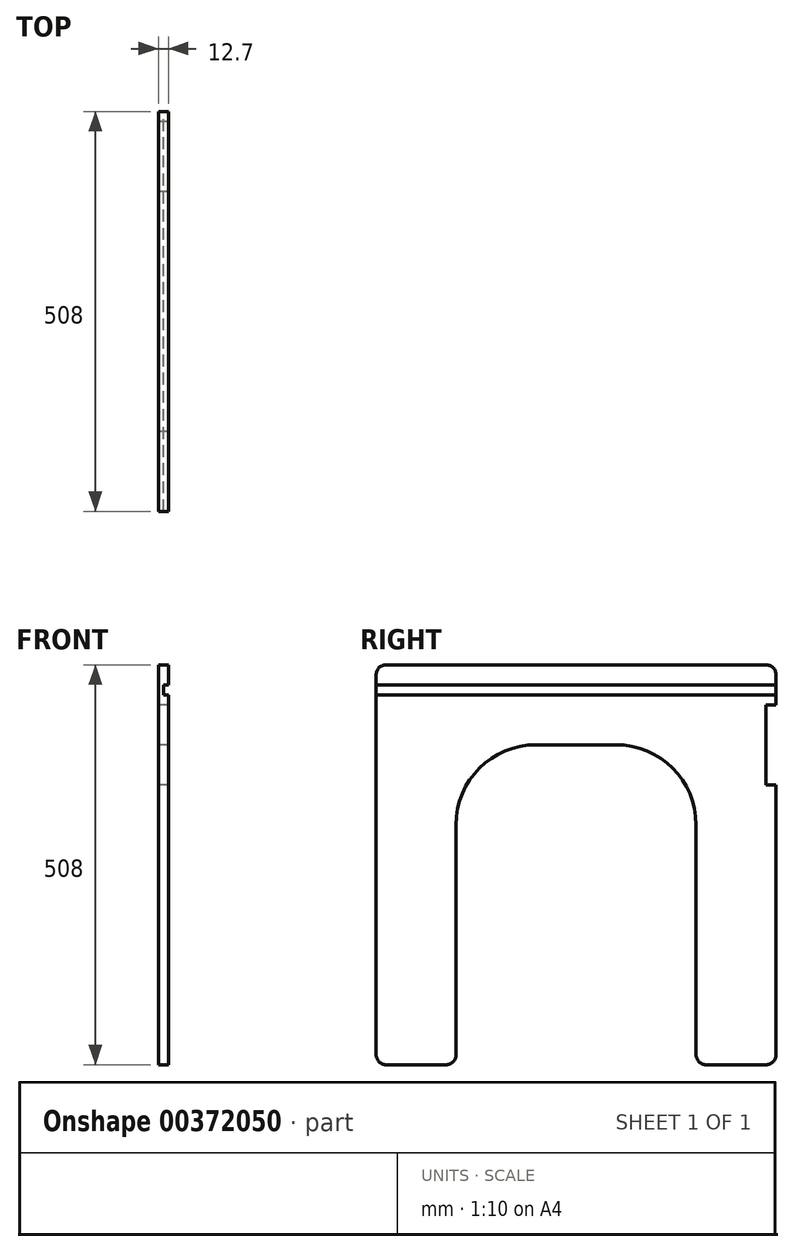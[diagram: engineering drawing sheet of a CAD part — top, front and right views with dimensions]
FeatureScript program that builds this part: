
annotation { "Feature Type Name" : "Feature", "Feature Type Description" : "" }
export const myFeature = defineFeature(function(context is Context, id is Id, definition is map)
    precondition{}
    {
        {
            var Q0;
            Q0=qCreatedBy(makeId("Right.planeOp"),FACE);
            var sketch = newSketch(context, id + "F0", { "sketchPlane" : qUnion([Q0])});
            skLineSegment(sketch, "E0.bottom", {"start": v(-88.9, 0) * mm, "end": v(-12.7, 0) * mm});
            skLineSegment(sketch, "E0.top", {"start": v(-88.9, 508) * mm, "end": v(393.7, 508) * mm});
            skLineSegment(sketch, "E0.left", {"start": v(-101.6, 12.7) * mm, "end": v(-101.6, 495.3) * mm});
            skLineSegment(sketch, "E0.right", {"start": v(406.4, 12.7) * mm, "end": v(406.4, 355.6) * mm});
            skLineSegment(sketch, "E1.top", {"start": v(203.2, 406.4) * mm, "end": v(101.6, 406.4) * mm});
            skLineSegment(sketch, "E1.left", {"start": v(304.8, 12.7) * mm, "end": v(304.8, 304.8) * mm});
            skLineSegment(sketch, "E1.right", {"start": v(0, 12.7) * mm, "end": v(0, 304.8) * mm});
            skPoint(sketch, "E2.visualSharp", {"position": v(0, 406.4) * mm});
            skArc(sketch, "E2.filletArc", {"start": v(101.6, 406.4) * mm, "mid": v(29.76, 376.64) * mm, "end": v(0, 304.8) * mm});
            skPoint(sketch, "E3.visualSharp", {"position": v(304.8, 406.4) * mm});
            skArc(sketch, "E3.filletArc", {"start": v(304.8, 304.8) * mm, "mid": v(275.04, 376.64) * mm, "end": v(203.2, 406.4) * mm});
            skPoint(sketch, "E4.visualSharp", {"position": v(-101.6, 0) * mm});
            skArc(sketch, "E4.filletArc", {"start": v(-101.6, 12.7) * mm, "mid": v(-97.88, 3.72) * mm, "end": v(-88.9, 0) * mm});
            skLineSegment(sketch, "E5.trimOffspring", {"start": v(317.5, 0) * mm, "end": v(393.7, 0) * mm});
            skPoint(sketch, "E6.visualSharp", {"position": v(0, 0) * mm});
            skArc(sketch, "E6.filletArc", {"start": v(-12.7, 0) * mm, "mid": v(-3.72, 3.72) * mm, "end": v(0, 12.7) * mm});
            skPoint(sketch, "E7.visualSharp", {"position": v(304.8, 0) * mm});
            skArc(sketch, "E7.filletArc", {"start": v(304.8, 12.7) * mm, "mid": v(308.52, 3.72) * mm, "end": v(317.5, 0) * mm});
            skPoint(sketch, "E8.visualSharp", {"position": v(406.4, 0) * mm});
            skArc(sketch, "E8.filletArc", {"start": v(393.7, 0) * mm, "mid": v(402.68, 3.72) * mm, "end": v(406.4, 12.7) * mm});
            skPoint(sketch, "E9.visualSharp", {"position": v(406.4, 508) * mm});
            skArc(sketch, "E9.filletArc", {"start": v(406.4, 495.3) * mm, "mid": v(402.68, 504.28) * mm, "end": v(393.7, 508) * mm});
            skPoint(sketch, "E10.visualSharp", {"position": v(-101.6, 508) * mm});
            skArc(sketch, "E10.filletArc", {"start": v(-88.9, 508) * mm, "mid": v(-97.88, 504.28) * mm, "end": v(-101.6, 495.3) * mm});
            skLineSegment(sketch, "E11.bottom", {"start": v(406.4, 457.2) * mm, "end": v(393.7, 457.2) * mm});
            skLineSegment(sketch, "E11.top", {"start": v(406.4, 355.6) * mm, "end": v(393.7, 355.6) * mm});
            skLineSegment(sketch, "E11.right", {"start": v(393.7, 457.2) * mm, "end": v(393.7, 355.6) * mm});
            skLineSegment(sketch, "E12.trimOffspring", {"start": v(406.4, 457.2) * mm, "end": v(406.4, 495.3) * mm});
            skSolve(sketch);
        }
        {
            var Q0;
            Q0=qSketchRegion(id+"F0",true);
            extrude(context, id + "F1", {"entities" : qUnion([Q0]), "depth" : 12.7 * mm});
        }
        {
            var Q0;
            Q0=makeQuery(id+"F1.opExtrude","CAP_FACE",FACE,{"disambiguationData":[OSD([sQuery(id+"F0.wireOp",EDGE,"E0.bottom"),sQuery(id+"F0.wireOp",EDGE,"E0.top"),sQuery(id+"F0.wireOp",EDGE,"E0.left"),sQuery(id+"F0.wireOp",EDGE,"E0.right"),sQuery(id+"F0.wireOp",EDGE,"E1.top"),sQuery(id+"F0.wireOp",EDGE,"E1.left"),sQuery(id+"F0.wireOp",EDGE,"E1.right"),sQuery(id+"F0.wireOp",EDGE,"E2.filletArc"),sQuery(id+"F0.wireOp",EDGE,"E3.filletArc"),sQuery(id+"F0.wireOp",EDGE,"E4.filletArc"),sQuery(id+"F0.wireOp",EDGE,"E5.trimOffspring"),sQuery(id+"F0.wireOp",EDGE,"E6.filletArc"),sQuery(id+"F0.wireOp",EDGE,"E7.filletArc"),sQuery(id+"F0.wireOp",EDGE,"E8.filletArc"),sQuery(id+"F0.wireOp",EDGE,"E9.filletArc"),sQuery(id+"F0.wireOp",EDGE,"E10.filletArc"),sQuery(id+"F0.wireOp",EDGE,"E11.bottom"),sQuery(id+"F0.wireOp",EDGE,"E11.top"),sQuery(id+"F0.wireOp",EDGE,"E11.right"),sQuery(id+"F0.wireOp",EDGE,"E12.trimOffspring")])],"isStart":false});
            var sketch = newSketch(context, id + "F2", { "sketchPlane" : qUnion([Q0])});
            skLineSegment(sketch, "E13.bottom", {"start": v(-101.6, 482.6) * mm, "end": v(406.4, 482.6) * mm});
            skLineSegment(sketch, "E13.top", {"start": v(-101.6, 469.9) * mm, "end": v(406.4, 469.9) * mm});
            skLineSegment(sketch, "E13.left", {"start": v(-101.6, 482.6) * mm, "end": v(-101.6, 469.9) * mm});
            skLineSegment(sketch, "E13.right", {"start": v(406.4, 482.6) * mm, "end": v(406.4, 469.9) * mm});
            skSolve(sketch);
        }
        {
            var Q0;
            Q0 = qSketchRegion(id + "F2", true);
            extrude(context, id + "F3", {"entities" : qUnion([Q0]), "operationType" : NewBodyOperationType.REMOVE, "oppositeDirection" : true, "depth" : 6.35 * mm});
        }
    });
